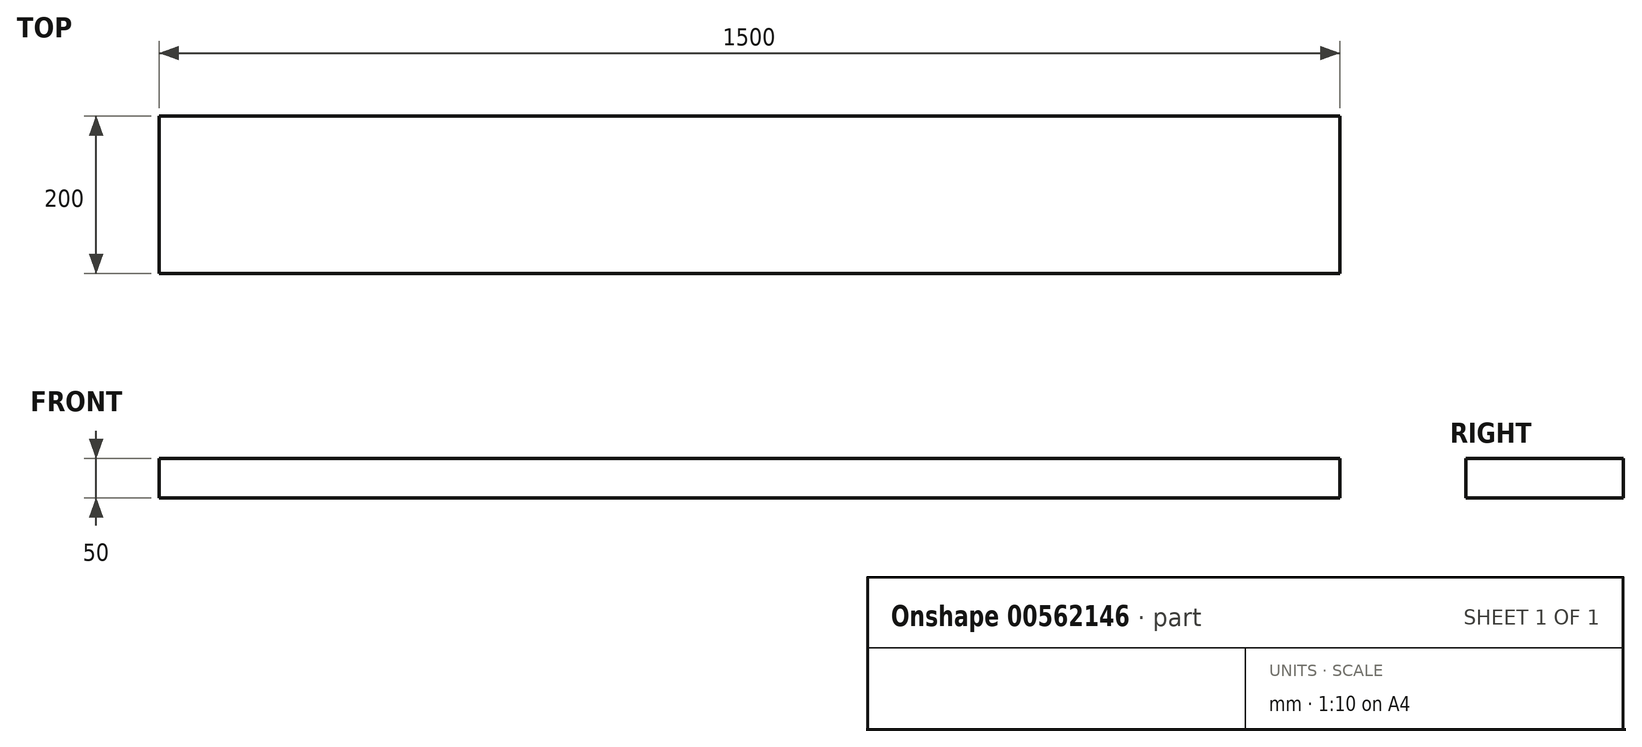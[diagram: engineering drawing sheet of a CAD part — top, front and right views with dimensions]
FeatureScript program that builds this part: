
annotation { "Feature Type Name" : "Feature", "Feature Type Description" : "" }
export const myFeature = defineFeature(function(context is Context, id is Id, definition is map)
    precondition{}
    {
        {
            var Q0;
            Q0=qCreatedBy(makeId("Top.planeOp"),FACE);
            var sketch = newSketch(context, id + "F0", { "sketchPlane" : qUnion([Q0])});
            skLineSegment(sketch, "E0.bottom", {"start": v(750, -100) * mm, "end": v(-750, -100) * mm});
            skLineSegment(sketch, "E0.top", {"start": v(750, 100) * mm, "end": v(-750, 100) * mm});
            skLineSegment(sketch, "E0.left", {"start": v(750, -100) * mm, "end": v(750, 100) * mm});
            skLineSegment(sketch, "E0.right", {"start": v(-750, -100) * mm, "end": v(-750, 100) * mm});
            skPoint(sketch, "E0.middle", {"position": v(0, 0) * mm});
            skSolve(sketch);
        }
        {
            var Q0;
            Q0 = qSketchRegion(id + "F0", true);
            extrude(context, id + "F1", {"entities" : qUnion([Q0]), "depth" : 50 * mm, "offsetDistance" : 25 * mm});
        }
    });
